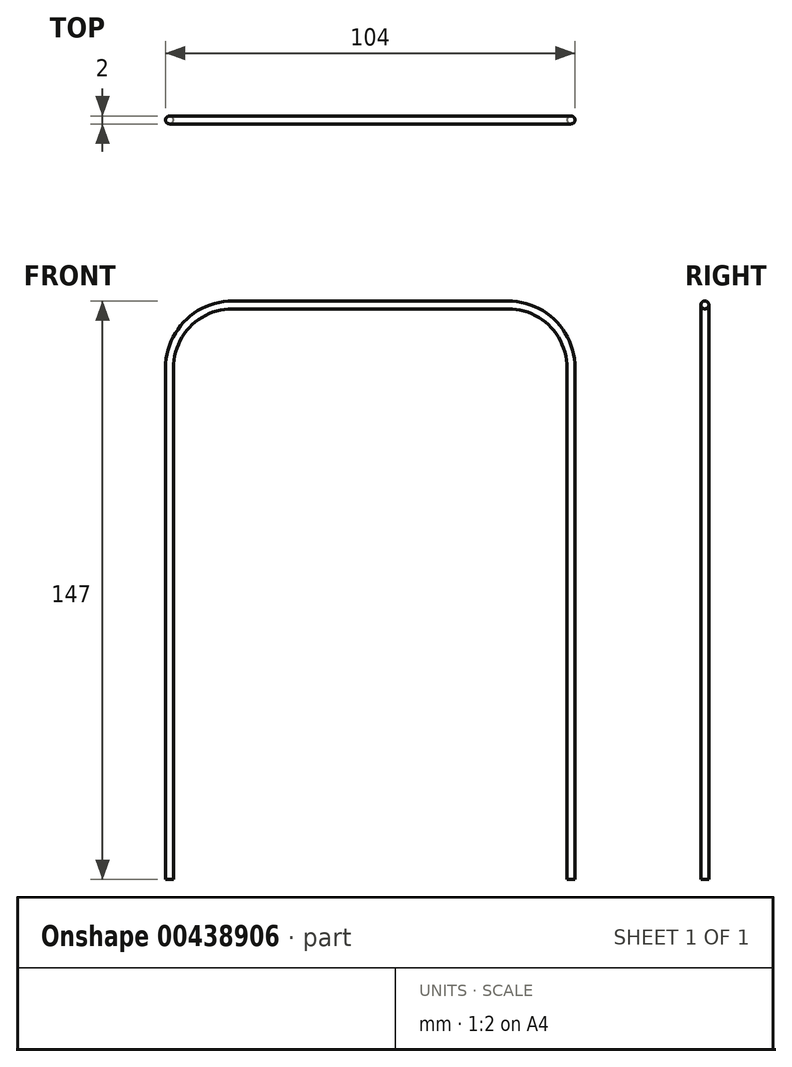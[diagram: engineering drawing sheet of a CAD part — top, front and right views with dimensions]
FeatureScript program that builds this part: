
annotation { "Feature Type Name" : "Feature", "Feature Type Description" : "" }
export const myFeature = defineFeature(function(context is Context, id is Id, definition is map)
    precondition{}
    {
        {
            var Q0;
            Q0=qCreatedBy(makeId("Front.planeOp"),FACE);
            var sketch = newSketch(context, id + "F0", { "sketchPlane" : qUnion([Q0])});
            skLineSegment(sketch, "E0", {"start": v(0, 0) * mm, "end": v(-35, 0) * mm});
            skLineSegment(sketch, "E1", {"start": v(-50, -15) * mm, "end": v(-50, -145) * mm});
            skPoint(sketch, "E2.visualSharp", {"position": v(-50, 0) * mm});
            skArc(sketch, "E2.filletArc", {"start": v(-35, 0) * mm, "mid": v(-45.6, -4.4) * mm, "end": v(-50, -15) * mm});
            skSolve(sketch);
        }
        {
            var Q0;
            Q0=qCreatedBy(makeId("Right.planeOp"),FACE);
            var sketch = newSketch(context, id + "F1", { "sketchPlane" : qUnion([Q0])});
            skCircle(sketch, "E3", {"center": v(0, 1) * mm, "radius": 1 * mm});
            skSolve(sketch);
        }
        {
            var Q0;
            Q0=makeQuery(id+"F1.imprint","IMPRINT",FACE,{"disambiguationData":[TD([[makeQuery(id+"F1.imprint","IMPRINT",EDGE,{"derivedFrom":sQuery(id+"F1.wireOp",EDGE,"E3")}),1.0]])]});
            var Q1;
            Q1=sQuery(id+"F0.wireOp",EDGE,"E0");
            var Q2;
            Q2=sQuery(id+"F0.wireOp",EDGE,"E2.filletArc");
            var Q3;
            Q3=sQuery(id+"F0.wireOp",EDGE,"E1");
            sweep(context, id + "F2", {"profiles" : qUnion([Q0]), "path" : qUnion([Q1, Q2, Q3])});
        }
        {
            var Q0;
            Q0=makeQuery(id+"F2.opSweep","SWEPT_BODY",BODY,{"disambiguationData":[OSD([sQuery(id+"F0.wireOp",EDGE,"E1"),sQuery(id+"F1.wireOp",EDGE,"E3")])]});
            var Q1;
            Q1=qCreatedBy(makeId("Right.planeOp"),FACE);
            mirror(context, id + "F3", {"operationType" : NewBodyOperationType.ADD, "entities" : qUnion([Q0]), "mirrorPlane" : qUnion([Q1])});
        }
    });
